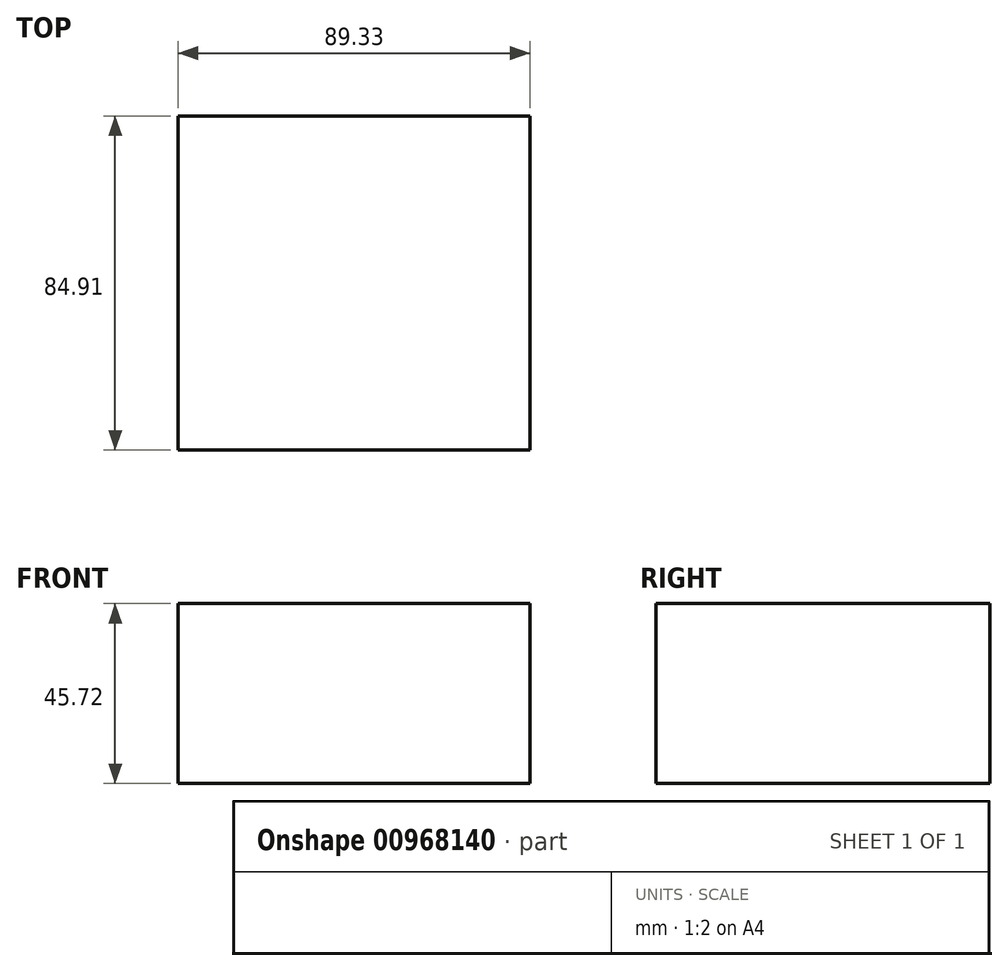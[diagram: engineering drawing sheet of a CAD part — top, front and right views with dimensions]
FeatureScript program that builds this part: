
annotation { "Feature Type Name" : "Feature", "Feature Type Description" : "" }
export const myFeature = defineFeature(function(context is Context, id is Id, definition is map)
    precondition{}
    {
        {
            var Q0;
            Q0=qCreatedBy(makeId("Top.planeOp"),FACE);
            var sketch = newSketch(context, id + "F0", { "sketchPlane" : qUnion([Q0])});
            skLineSegment(sketch, "E0.bottom", {"start": v(0, 0) * mm, "end": v(-89.33, 0) * mm});
            skLineSegment(sketch, "E0.top", {"start": v(0, -84.9) * mm, "end": v(-89.33, -84.9) * mm});
            skLineSegment(sketch, "E0.left", {"start": v(0, 0) * mm, "end": v(0, -84.9) * mm});
            skLineSegment(sketch, "E0.right", {"start": v(-89.33, 0) * mm, "end": v(-89.33, -84.9) * mm});
            skSolve(sketch);
        }
        {
            var Q0;
            Q0=makeQuery(id+"F0.imprint","IMPRINT",FACE,{"disambiguationData":[TD([[makeQuery(id+"F0.imprint","IMPRINT",EDGE,{"derivedFrom":sQuery(id+"F0.wireOp",EDGE,"E0.bottom")}),1.0]])]});
            extrude(context, id + "F1", {"entities" : qUnion([Q0]), "depth" : 45.72 * mm, "offsetDistance" : 25.4 * mm});
        }
    });
